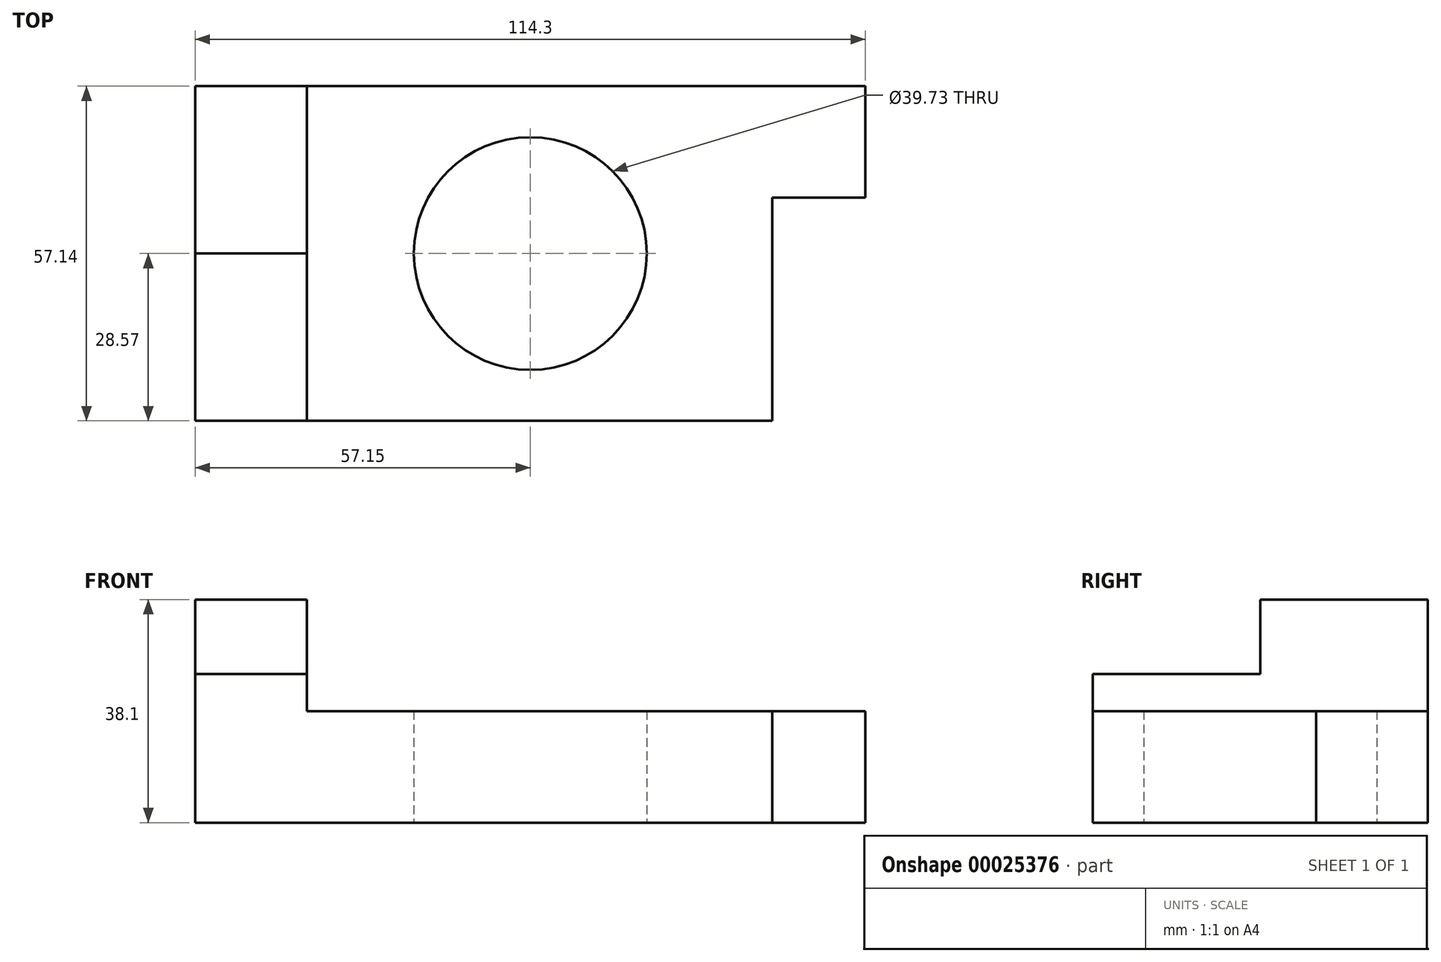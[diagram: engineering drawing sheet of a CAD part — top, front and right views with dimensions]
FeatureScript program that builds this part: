
annotation { "Feature Type Name" : "Feature", "Feature Type Description" : "" }
export const myFeature = defineFeature(function(context is Context, id is Id, definition is map)
    precondition{}
    {
        {
            var Q0;
            Q0=qCreatedBy(makeId("Top.planeOp"),FACE);
            var sketch = newSketch(context, id + "F0", { "sketchPlane" : qUnion([Q0])});
            skLineSegment(sketch, "E0.bottom", {"start": v(-57.15, 28.58) * mm, "end": v(57.15, 28.58) * mm});
            skLineSegment(sketch, "E0.top", {"start": v(-57.15, -28.57) * mm, "end": v(41.28, -28.57) * mm});
            skLineSegment(sketch, "E0.left", {"start": v(-57.15, 28.58) * mm, "end": v(-57.15, -28.57) * mm});
            skLineSegment(sketch, "E0.right", {"start": v(57.15, 28.58) * mm, "end": v(57.15, 9.53) * mm});
            skLineSegment(sketch, "E1", {"start": v(41.28, -28.57) * mm, "end": v(41.28, 9.53) * mm});
            skLineSegment(sketch, "E2", {"start": v(41.28, 9.53) * mm, "end": v(57.15, 9.53) * mm});
            skCircle(sketch, "E3", {"center": v(0, 0) * mm, "radius": 19.86 * mm});
            skLineSegment(sketch, "E4", {"start": v(-38.1, 28.58) * mm, "end": v(-38.1, -28.57) * mm});
            skLineSegment(sketch, "E5", {"start": v(-57.15, 0) * mm, "end": v(-38.1, 0) * mm});
            skSolve(sketch);
        }
        {
            var Q0;
            {var subQ7=sQuery(id+"F0.wireOp",EDGE,"E0.right");Q0=makeQuery(id+"F0.imprint","IMPRINT",FACE,{"disambiguationData":[TD([[makeQuery(id+"F0.imprint","IMPRINT",EDGE,{"derivedFrom":subQ7}),-1.0]])]});}
            extrude(context, id + "F1", {"entities" : qUnion([Q0]), "depth" : 19.05 * mm});
        }
        {
            var Q0;
            {var subQ0=sQuery(id+"F0.wireOp",EDGE,"E5");Q0=makeQuery(id+"F0.imprint","IMPRINT",FACE,{"disambiguationData":[TD([[makeQuery(id+"F0.imprint","IMPRINT",EDGE,{"derivedFrom":subQ0}),1.0]])]});}
            extrude(context, id + "F2", {"entities" : qUnion([Q0]), "operationType" : NewBodyOperationType.ADD, "depth" : 38.1 * mm});
        }
        {
            var Q0;
            {var subQ0=sQuery(id+"F0.wireOp",EDGE,"E5");Q0=makeQuery(id+"F0.imprint","IMPRINT",FACE,{"disambiguationData":[TD([[makeQuery(id+"F0.imprint","IMPRINT",EDGE,{"derivedFrom":subQ0}),-1.0]])]});}
            extrude(context, id + "F3", {"entities" : qUnion([Q0]), "operationType" : NewBodyOperationType.ADD, "depth" : 25.4 * mm});
        }
    });
